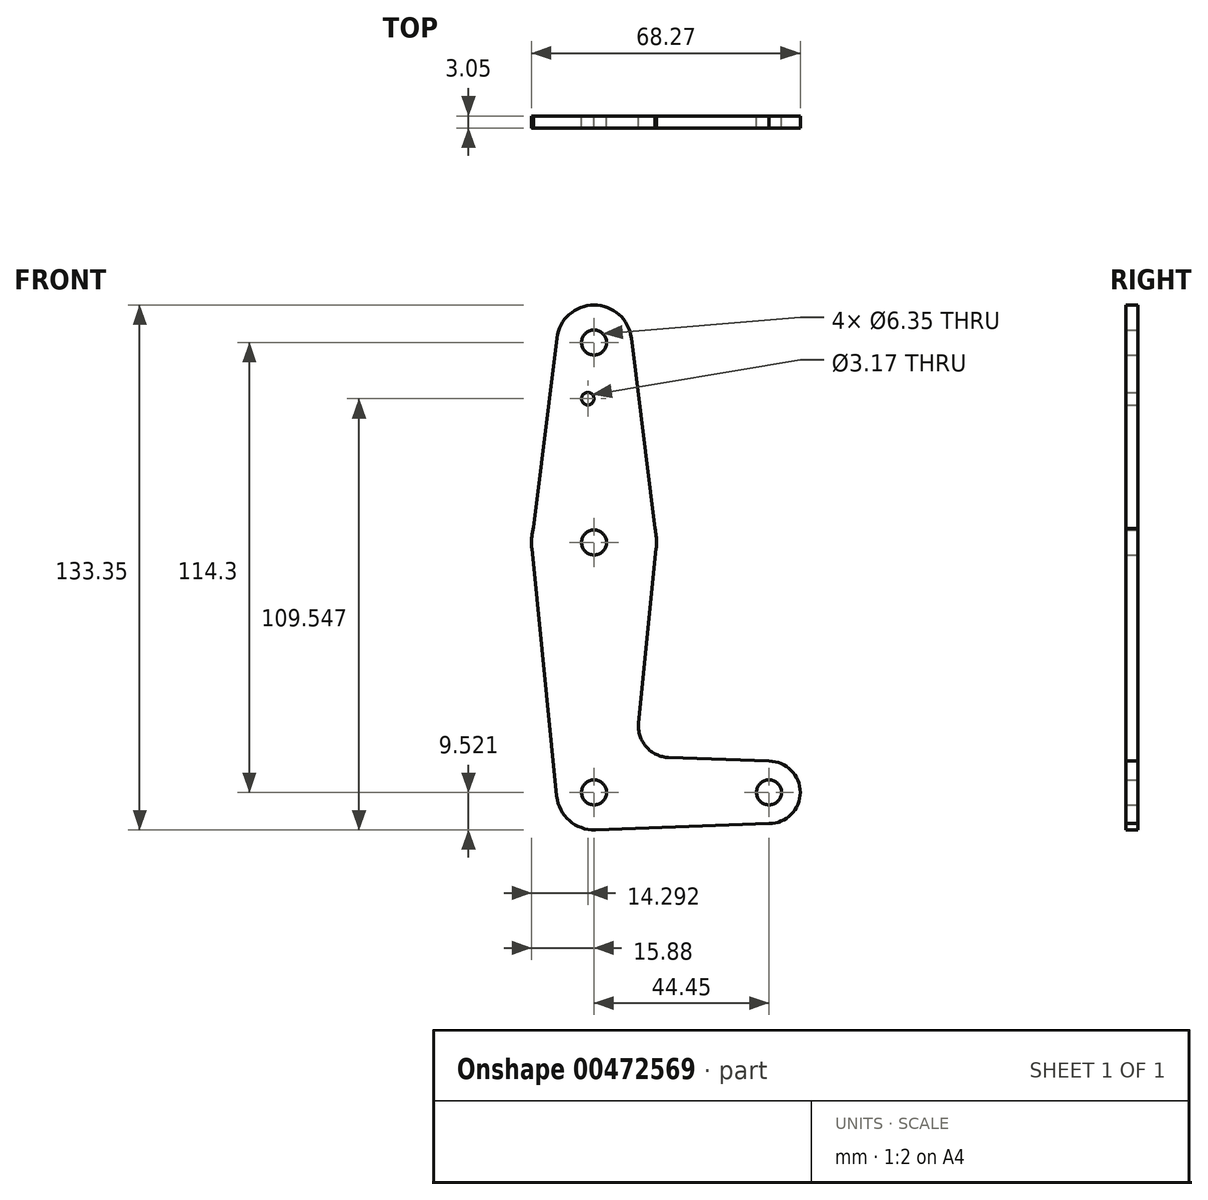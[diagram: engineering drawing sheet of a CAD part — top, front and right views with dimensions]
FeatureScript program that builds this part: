
annotation { "Feature Type Name" : "Feature", "Feature Type Description" : "" }
export const myFeature = defineFeature(function(context is Context, id is Id, definition is map)
    precondition{}
    {
        {
            var Q0;
            Q0=qCreatedBy(makeId("Front.planeOp"),FACE);
            var sketch = newSketch(context, id + "F0", { "sketchPlane" : qUnion([Q0])});
            skLineSegment(sketch, "E0", {"start": v(-44.45, -70.18) * mm, "end": v(0, -70.18) * mm, "construction": true});
            skCircle(sketch, "E1", {"center": v(-44.45, 44.12) * mm, "radius": 9.53 * mm});
            skCircle(sketch, "E2", {"center": v(-44.45, -70.18) * mm, "radius": 9.53 * mm});
            skCircle(sketch, "E3", {"center": v(0, -70.18) * mm, "radius": 7.94 * mm});
            skLineSegment(sketch, "E4", {"start": v(-44.45, 44.12) * mm, "end": v(-44.45, -70.18) * mm, "construction": true});
            skCircle(sketch, "E5", {"center": v(-44.45, -6.68) * mm, "radius": 15.88 * mm});
            skLineSegment(sketch, "E6", {"start": v(-60.25, -8.27) * mm, "end": v(-53.93, -71.13) * mm});
            skLineSegment(sketch, "E7", {"start": v(-28.65, -8.27) * mm, "end": v(-33.1, -52.59) * mm});
            skLineSegment(sketch, "E8", {"start": v(-25.48, -61.33) * mm, "end": v(0, -62.24) * mm});
            skLineSegment(sketch, "E9", {"start": v(0, -62.24) * mm, "end": v(0, -78.12) * mm});
            skLineSegment(sketch, "E10", {"start": v(0, -78.12) * mm, "end": v(-44.1, -79.7) * mm});
            skCircle(sketch, "E11", {"center": v(-44.45, 44.12) * mm, "radius": 3.18 * mm});
            skCircle(sketch, "E12", {"center": v(-44.45, -6.68) * mm, "radius": 3.18 * mm});
            skCircle(sketch, "E13", {"center": v(-44.45, -70.18) * mm, "radius": 3.17 * mm});
            skCircle(sketch, "E14", {"center": v(0, -70.18) * mm, "radius": 3.17 * mm});
            skCircle(sketch, "E15", {"center": v(-46.04, 29.85) * mm, "radius": 1.59 * mm});
            skArc(sketch, "E16.filletArc", {"start": v(-33.1, -52.59) * mm, "mid": v(-31.19, -58.61) * mm, "end": v(-25.48, -61.33) * mm});
            skLineSegment(sketch, "E17", {"start": v(-59.86, -2.88) * mm, "end": v(-53.9, 45.3) * mm});
            skLineSegment(sketch, "E18", {"start": v(-28.96, -3.19) * mm, "end": v(-35, 45.3) * mm});
            skSolve(sketch);
        }
        {
            var Q0;
            Q0 = qSketchRegion(id + "F0", true);
            extrude(context, id + "F1", {"entities" : qUnion([Q0]), "depth" : 3.05 * mm});
        }
    });
